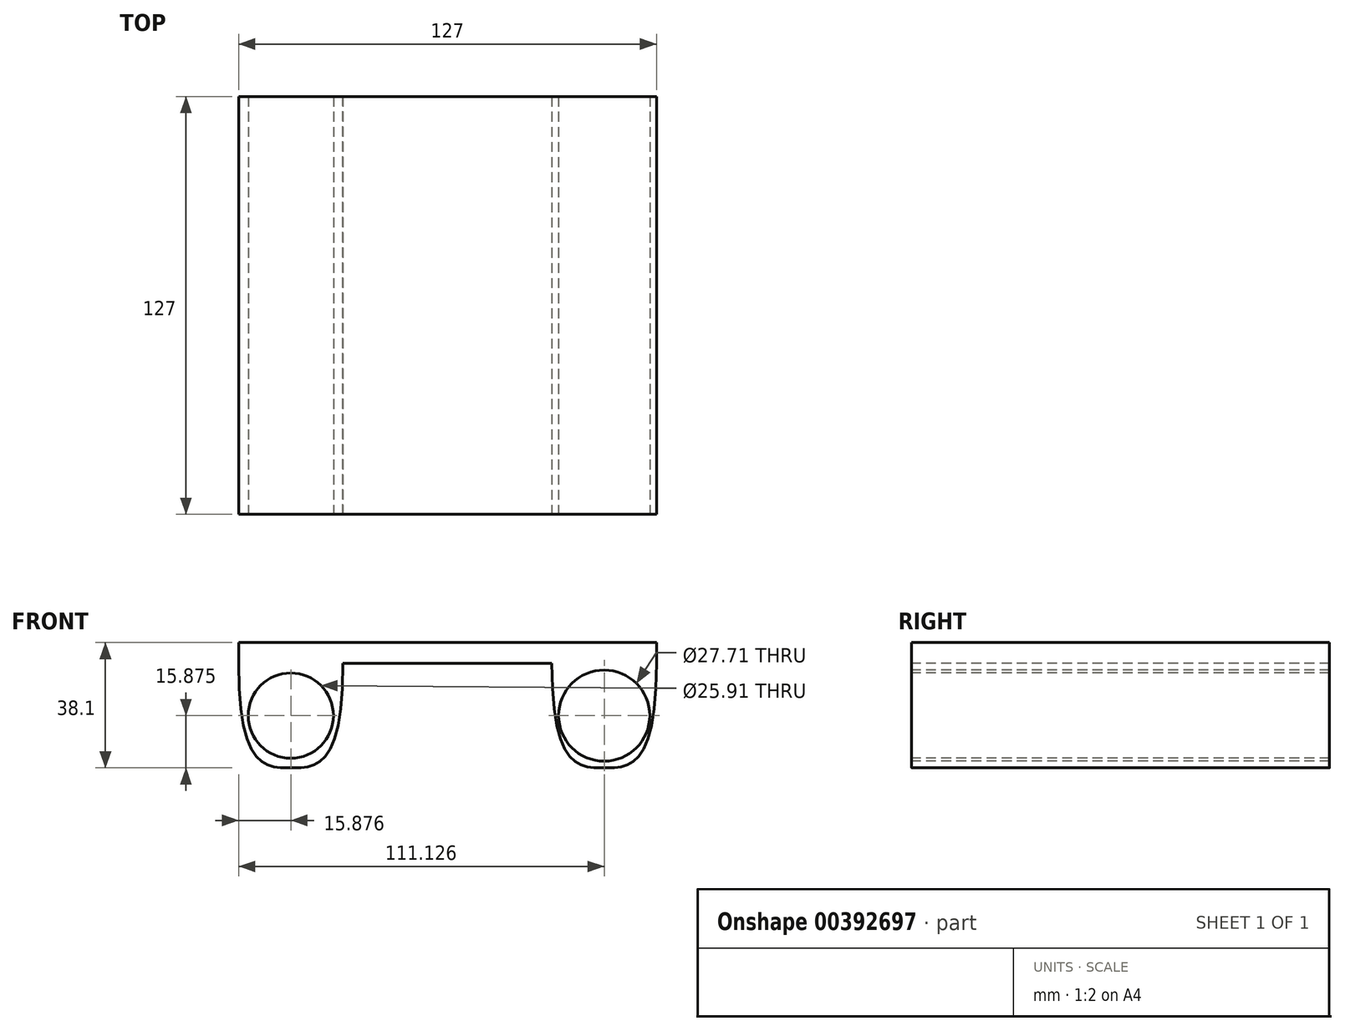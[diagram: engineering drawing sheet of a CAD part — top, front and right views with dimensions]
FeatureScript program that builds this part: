
annotation { "Feature Type Name" : "Feature", "Feature Type Description" : "" }
export const myFeature = defineFeature(function(context is Context, id is Id, definition is map)
    precondition{}
    {
        {
            var Q0;
            Q0=qCreatedBy(makeId("Front.planeOp"),FACE);
            var sketch = newSketch(context, id + "F0", { "sketchPlane" : qUnion([Q0])});
            skLineSegment(sketch, "E0.bottom", {"start": v(-75.69, 0) * mm, "end": v(51.31, 0) * mm});
            skLineSegment(sketch, "E0.top", {"start": v(-75.69, 6.35) * mm, "end": v(51.31, 6.35) * mm});
            skLineSegment(sketch, "E0.left", {"start": v(-75.69, 0) * mm, "end": v(-75.69, 6.35) * mm});
            skLineSegment(sketch, "E0.right", {"start": v(51.31, 0) * mm, "end": v(51.31, 6.35) * mm});
            skFitSpline(sketch, "E1", {"points": [v(51.31, 0) * mm, v(35.44, -31.75) * mm, v(19.56, 0) * mm], "startDerivative": vector(0, -190.5) * mm, "endDerivative": vector(0, 190.5) * mm});
            skFitSpline(sketch, "E2", {"points": [v(-75.69, 0) * mm, v(-59.81, -31.75) * mm, v(-43.94, 0) * mm], "startDerivative": vector(0.05, -190.5) * mm, "endDerivative": vector(-0.05, 190.5) * mm});
            skSolve(sketch);
        }
        {
            var Q0;
            Q0=makeQuery(id+"F0.imprint","IMPRINT",FACE,{"disambiguationData":[TD([[makeQuery(id+"F0.imprint","IMPRINT",EDGE,{"derivedFrom":sQuery(id+"F0.wireOp",EDGE,"E0.top")}),-1.0]])]});
            extrude(context, id + "F1", {"entities" : qUnion([Q0]), "oppositeDirection" : true, "depth" : 63.5 * mm});
        }
        {
            var Q0;
            Q0=makeQuery(id+"F1.opExtrude","CAP_EDGE",EDGE,{"disambiguationData":[OSD([sQuery(id+"F0.wireOp",EDGE,"E0.top")])],"isStart":false});
            cPlane(context, id + "F2", {"entities" : qUnion([Q0]), "cplaneType" : CPlaneType.LINE_ANGLE, "offset" : 25.4 * mm, "angle" : 0 * degree, "width" : 152.4 * mm, "height" : 152.4 * mm});
        }
        {
            var Q0;
            {var subQ0=sQuery(id+"F0.wireOp",EDGE,"E1");Q0=makeQuery(id+"F0.imprint","IMPRINT",FACE,{"disambiguationData":[TD([[makeQuery(id+"F0.imprint","IMPRINT",EDGE,{"derivedFrom":subQ0}),-1.0]])]});}
            var Q1;
            {var subQ0=sQuery(id+"F0.wireOp",EDGE,"E2");Q1=makeQuery(id+"F0.imprint","IMPRINT",FACE,{"disambiguationData":[TD([[makeQuery(id+"F0.imprint","IMPRINT",EDGE,{"derivedFrom":subQ0}),1.0]])]});}
            extrude(context, id + "F3", {"entities" : qUnion([Q0, Q1]), "operationType" : NewBodyOperationType.ADD, "oppositeDirection" : true, "depth" : 63.5 * mm});
        }
        {
            var Q0;
            Q0=makeQuery(id+"F1.opExtrude","SWEPT_BODY",BODY,{"disambiguationData":[OSD([sQuery(id+"F0.wireOp",EDGE,"E0.bottom"),sQuery(id+"F0.wireOp",EDGE,"E0.top"),sQuery(id+"F0.wireOp",EDGE,"E0.left"),sQuery(id+"F0.wireOp",EDGE,"E0.right")])]});
            var Q1;
            Q1=qCreatedBy(id+"F2.planeOp",FACE);
            mirror(context, id + "F4", {"operationType" : NewBodyOperationType.ADD, "entities" : qUnion([Q0]), "mirrorPlane" : qUnion([Q1])});
        }
        {
            var Q0;
            {var subQ0=sQuery(id+"F0.wireOp",EDGE,"E1");Q0=makeQuery(id+"F0.imprint","IMPRINT",FACE,{"disambiguationData":[TD([[makeQuery(id+"F0.imprint","IMPRINT",EDGE,{"derivedFrom":subQ0}),-1.0]])]});}
            var sketch = newSketch(context, id + "F5", { "sketchPlane" : qUnion([Q0])});
            skCircle(sketch, "E3", {"center": v(35.44, -15.88) * mm, "radius": 13.85 * mm});
            skSolve(sketch);
        }
        {
            var Q0;
            Q0 = qSketchRegion(id + "F5", true);
            extrude(context, id + "F6", {"entities" : qUnion([Q0]), "operationType" : NewBodyOperationType.REMOVE, "oppositeDirection" : true, "depth" : 127 * mm});
        }
        {
            var Q0;
            {var subQ0=sQuery(id+"F0.wireOp",EDGE,"E2");Q0=makeQuery(id+"F0.imprint","IMPRINT",FACE,{"disambiguationData":[TD([[makeQuery(id+"F0.imprint","IMPRINT",EDGE,{"derivedFrom":subQ0}),1.0]])]});}
            var sketch = newSketch(context, id + "F7", { "sketchPlane" : qUnion([Q0])});
            skCircle(sketch, "E4", {"center": v(-59.81, -15.88) * mm, "radius": 12.95 * mm});
            skSolve(sketch);
        }
        {
            var Q0;
            Q0 = qSketchRegion(id + "F7", true);
            extrude(context, id + "F8", {"entities" : qUnion([Q0]), "operationType" : NewBodyOperationType.REMOVE, "oppositeDirection" : true, "depth" : 127 * mm});
        }
    });
